# Revit family: CENTUM Gabelkopf 16x64_
name_source: partatom
category: HLS-Bauteile
revit_build: Autodesk Revit 2018 (Build: 20190510_1515(x64)
units: mm (PartAtom-declared; Revit-internal decimal feet)

## family parameters
Arbeitsebenenbasiert = Ja
Beim Laden mit Abzugskörper schneiden = Nein
Bemaßung runder Anschluss = Durchmesser verwenden
Gemeinsam genutzt = Ja
Immer vertikal = Nein
Raumberechnungspunkt = Nein
Teiletyp = Normal

## types (1)
- CENTUM Gabelkopf 16x64_
    Artikelnummer = 1660007316
    EAN = 4250928449504
    Fabrikat = MEFA
    Firma = MEFA Befestigungs- und Montagesysteme GmbH
    Gewicht = 0.41 kg
    Gewicht pro Bauteil = 0.41 kg
    Gewinde = M16
    Höhe = 32 mm
    Kurztext1 = Gabelkopf M16 DIN 71752
    Kurztext2 = 16 mm x 64 mm
    Lochdurchmesser = 16 mm
    Material = Stahl
    Mengeneinheit = St
    Oberflaeche = galvanisch verzinkt
    Randabstand Lochung c = 64 mm
    Randabstand Lochung d = 96 mm
    Schlitzhöhe = 16 mm
    Vorgabe-Ansicht = 1219 mm
    max. zul. Last = 20.00 kN
    vpe = 5 St
